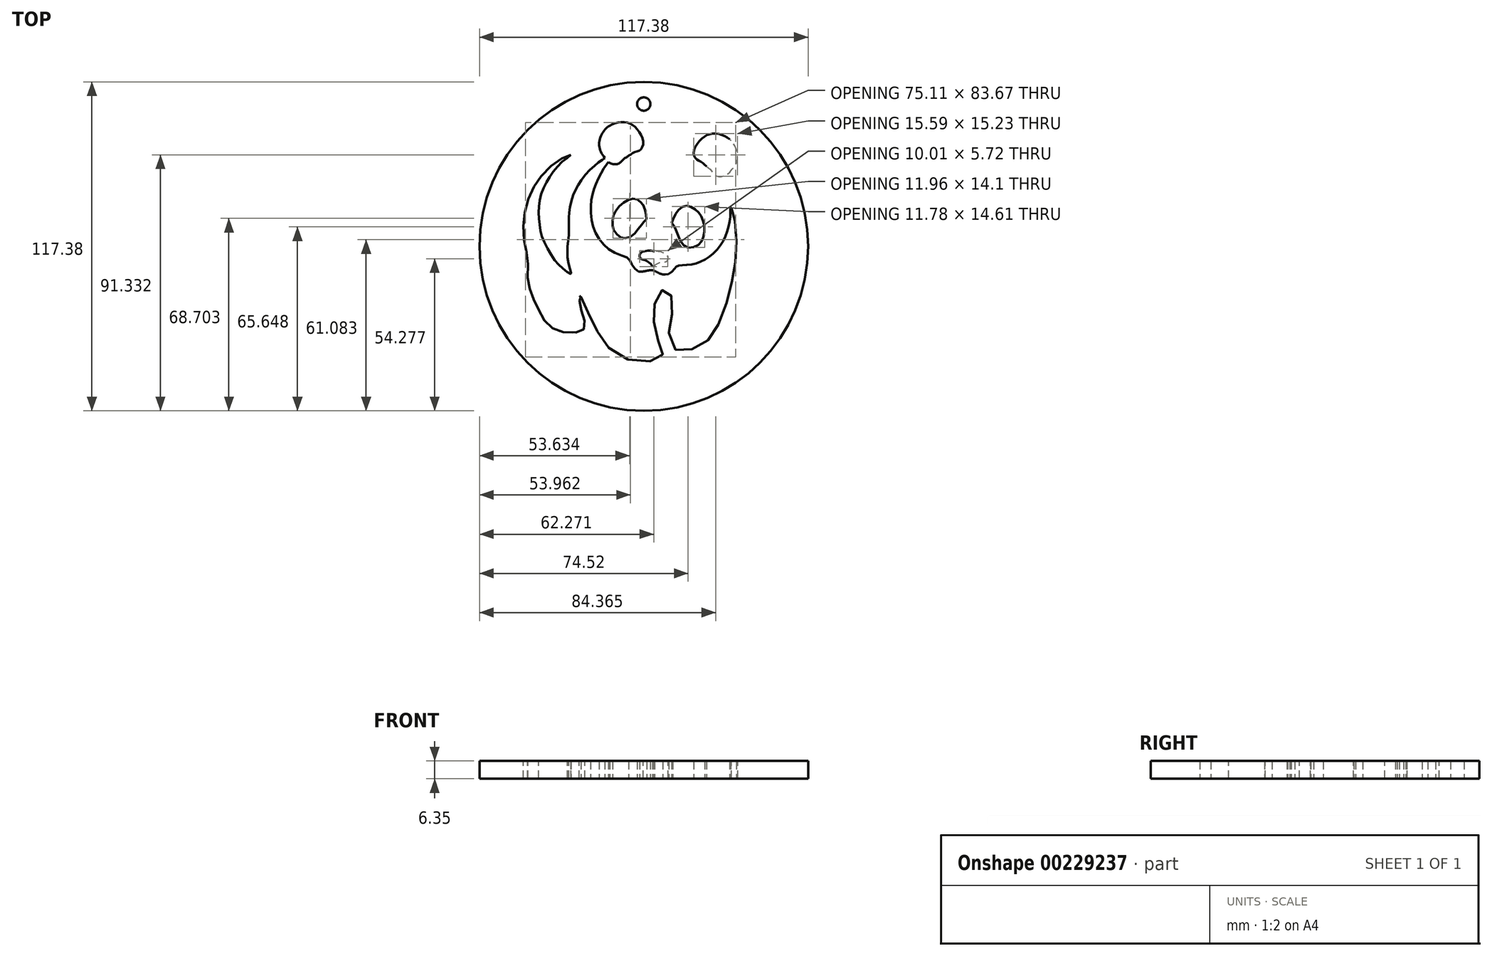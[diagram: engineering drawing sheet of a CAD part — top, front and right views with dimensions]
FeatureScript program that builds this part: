
annotation { "Feature Type Name" : "Feature", "Feature Type Description" : "" }
export const myFeature = defineFeature(function(context is Context, id is Id, definition is map)
    precondition{}
    {
        {
            var Q0;
            Q0=qCreatedBy(makeId("Top.planeOp"),FACE);
            var sketch = newSketch(context, id + "F0", { "sketchPlane" : qUnion([Q0])});
            skFitSpline(sketch, "E0", {"points": [v(-9.45, -0.21) * mm, v(-9.65, 1.94) * mm, v(-10.1, 4.07) * mm, v(-11.24, 5.8) * mm, v(-12.39, 6.69) * mm, v(-13.82, 7.25) * mm, v(-16.1, 6.73) * mm, v(-18.02, 5.5) * mm, v(-19.95, 3.49) * mm, v(-21.27, 0.9) * mm, v(-21.48, -1.33) * mm, v(-21.32, -3.3) * mm, v(-20.37, -5.07) * mm, v(-18.44, -6.7) * mm, v(-16.78, -6.87) * mm, v(-14.6, -6.12) * mm, v(-12.36, -3.6) * mm, v(-11.05, -1.96) * mm, v(-10.27, -0.98) * mm, v(-9.45, -0.21) * mm]});
            skLineSegment(sketch, "E1", {"start": v(-7.13, -17.08) * mm, "end": v(-6.54, -11.5) * mm, "construction": true});
            skFitSpline(sketch, "E2", {"points": [v(-7.13, -17.08) * mm, v(-6.61, -16.68) * mm, v(-6.27, -16.39) * mm, v(-5.51, -15.93) * mm, v(-4.62, -15.58) * mm, v(-3.6, -15.41) * mm, v(-2.85, -15.39) * mm, v(-2.06, -15) * mm, v(-1.7, -14.33) * mm, v(-1.68, -13.65) * mm, v(-2.14, -12.86) * mm, v(-3.15, -12.2) * mm, v(-4.37, -11.82) * mm, v(-5.34, -11.65) * mm, v(-6.54, -11.5) * mm], "startDerivative": vector(8.27, 4.27) * mm, "endDerivative": vector(-8.57, -0.03) * mm});
            skFitSpline(sketch, "E3.MirrorCS", {"points": [v(-7.13, -17.08) * mm, v(-7.55, -16.58) * mm, v(-7.82, -16.22) * mm, v(-8.47, -15.61) * mm, v(-9.27, -15.08) * mm, v(-10.24, -14.7) * mm, v(-10.96, -14.52) * mm, v(-11.65, -13.98) * mm, v(-11.87, -13.25) * mm, v(-11.74, -12.59) * mm, v(-11.12, -11.9) * mm, v(-10, -11.48) * mm, v(-8.73, -11.36) * mm, v(-7.74, -11.4) * mm, v(-6.54, -11.5) * mm], "startDerivative": vector(-7.19, 5.91) * mm, "endDerivative": vector(8.37, -1.83) * mm});
            skLineSegment(sketch, "E4", {"start": v(12, 18.82) * mm, "end": v(20.22, 28.44) * mm, "construction": true});
            skFitSpline(sketch, "E5", {"points": [v(12, 18.82) * mm, v(12.77, 18.12) * mm, v(13.56, 17.43) * mm, v(14.25, 16.5) * mm, v(14.91, 15.73) * mm, v(15.82, 15.22) * mm, v(17.04, 15.04) * mm, v(18.74, 15.54) * mm, v(20.57, 17) * mm, v(22.03, 18.82) * mm, v(22.87, 20.59) * mm, v(23.15, 22.16) * mm, v(22.91, 24.11) * mm, v(22.24, 25.86) * mm, v(21.34, 27.32) * mm, v(20.22, 28.44) * mm], "startDerivative": vector(13.61, -13.3) * mm, "endDerivative": vector(-19.87, 13.26) * mm});
            skFitSpline(sketch, "E6.MirrorCS", {"points": [v(12, 18.82) * mm, v(11.19, 19.46) * mm, v(10.39, 20.14) * mm, v(9.37, 20.68) * mm, v(8.5, 21.21) * mm, v(7.85, 22.02) * mm, v(7.49, 23.2) * mm, v(7.7, 24.96) * mm, v(8.87, 27) * mm, v(10.44, 28.72) * mm, v(12.05, 29.83) * mm, v(13.56, 30.35) * mm, v(15.53, 30.42) * mm, v(17.35, 30.04) * mm, v(18.93, 29.37) * mm, v(20.22, 28.44) * mm], "startDerivative": vector(-15.26, 11.37) * mm, "endDerivative": vector(16.2, -17.55) * mm});
            skFitSpline(sketch, "E7", {"points": [v(-15.77, 22.56) * mm, v(-14.87, 23.07) * mm, v(-13.98, 23.62) * mm, v(-12.9, 24) * mm, v(-11.96, 24.41) * mm, v(-11.2, 25.12) * mm, v(-10.67, 26.24) * mm, v(-10.63, 28) * mm, v(-11.48, 30.19) * mm, v(-12.79, 32.12) * mm, v(-14.22, 33.45) * mm, v(-15.64, 34.18) * mm, v(-17.57, 34.54) * mm, v(-19.43, 34.42) * mm, v(-21.1, 34) * mm, v(-22.5, 33.26) * mm], "startDerivative": vector(16.75, 9.03) * mm, "endDerivative": vector(-18.57, -15.02) * mm});
            skFitSpline(sketch, "E8.MirrorCS", {"points": [v(-15.77, 22.56) * mm, v(-16.63, 21.97) * mm, v(-17.51, 21.4) * mm, v(-18.33, 20.59) * mm, v(-19.1, 19.92) * mm, v(-20.07, 19.54) * mm, v(-21.3, 19.55) * mm, v(-22.91, 20.28) * mm, v(-24.5, 22) * mm, v(-25.7, 24.01) * mm, v(-26.26, 25.88) * mm, v(-26.31, 27.47) * mm, v(-25.8, 29.37) * mm, v(-24.88, 31) * mm, v(-23.78, 32.32) * mm, v(-22.5, 33.26) * mm], "startDerivative": vector(-15.4, -11.18) * mm, "endDerivative": vector(21.58, 10.23) * mm});
            skFitSpline(sketch, "E9", {"points": [v(-22.97, 20.33) * mm, v(-23.35, 19.77) * mm, v(-24.07, 18.85) * mm, v(-25.06, 17.32) * mm, v(-26.24, 15.22) * mm, v(-27.42, 12.67) * mm, v(-28.12, 10.8) * mm, v(-28.63, 9) * mm, v(-29.16, 5.98) * mm, v(-29.33, 3.24) * mm, v(-29, -0.56) * mm, v(-28.2, -3.56) * mm, v(-26.63, -6.7) * mm, v(-24.33, -9.54) * mm, v(-21.64, -11.65) * mm, v(-17.98, -13.23) * mm, v(-16.1, -13.91) * mm, v(-15.16, -15.07) * mm, v(-14.66, -16.27) * mm, v(-13.47, -17.96) * mm, v(-12.17, -18.8) * mm, v(-10.25, -18.71) * mm, v(-8.8, -18.43) * mm, v(-7.33, -18.35) * mm], "startDerivative": vector(-14.05, -22.2) * mm, "endDerivative": vector(35.9, -3.85) * mm});
            skFitSpline(sketch, "E10", {"points": [v(-7.33, -18.35) * mm, v(-6.65, -18.52) * mm, v(-5.91, -18.87) * mm, v(-5.28, -19.2) * mm, v(-4.42, -19.57) * mm, v(-3.54, -19.83) * mm, v(-2.7, -19.9) * mm, v(-1.5, -19.71) * mm, v(0.34, -18.14) * mm, v(0.9, -17.44) * mm, v(1.6, -16.87) * mm, v(2.49, -16.64) * mm, v(4.5, -16.48) * mm, v(7.18, -16.17) * mm, v(9.84, -15.3) * mm, v(12.44, -13.88) * mm, v(14.95, -11.87) * mm, v(17.14, -9.23) * mm, v(18.72, -6.45) * mm, v(19.8, -3.14) * mm, v(20.4, -0.4) * mm, v(20.5, 2.19) * mm, v(20.64, 4.02) * mm], "startDerivative": vector(22.76, -4.55) * mm, "endDerivative": vector(10, 38.6) * mm});
            skFitSpline(sketch, "E11", {"points": [v(20.64, 4.02) * mm, v(21.2, 3.69) * mm, v(21.77, 1.66) * mm, v(22.13, -0.21) * mm, v(22.44, -2.66) * mm, v(22.69, -7.22) * mm, v(22.62, -11.45) * mm, v(22.31, -15.8) * mm, v(21.5, -20.19) * mm, v(20.93, -23.17) * mm, v(20.14, -26.46) * mm, v(18.07, -33.4) * mm, v(16.45, -37.25) * mm, v(14.83, -40.35) * mm, v(12.93, -42.9) * mm, v(10.64, -44.82) * mm, v(7.36, -46.34) * mm, v(4.4, -46.96) * mm, v(1.93, -46.94) * mm, v(0, -46.07) * mm, v(-1.45, -42.28) * mm, v(-0.97, -38.56) * mm, v(-0.39, -35.07) * mm, v(-0.1, -32.63) * mm, v(-0.2, -28.84) * mm, v(-1.07, -26.34) * mm, v(-2.24, -25.37) * mm, v(-3.28, -25.17) * mm, v(-4.92, -26.4) * mm, v(-5.99, -28.5) * mm, v(-6.74, -31.2) * mm, v(-6.82, -34) * mm, v(-6.71, -37.34) * mm, v(-6.15, -40.5) * mm, v(-4.87, -44.43) * mm, v(-3.86, -46.44) * mm, v(-3.58, -47.98) * mm, v(-3.9, -49.07) * mm, v(-5.6, -50.27) * mm, v(-9, -50.97) * mm, v(-13.7, -50.8) * mm, v(-18.32, -49.26) * mm, v(-22.46, -46.36) * mm, v(-24.72, -43.76) * mm, v(-27.06, -40.02) * mm, v(-29.02, -36.25) * mm, v(-30.7, -32.5) * mm, v(-32.06, -29.5) * mm, v(-32.79, -27.9) * mm], "startDerivative": vector(61.87, -18.92) * mm, "endDerivative": vector(-42.49, 93.36) * mm});
            skFitSpline(sketch, "E12", {"points": [v(-24.32, 21.75) * mm, v(-25.03, 21.24) * mm, v(-26.64, 20.08) * mm, v(-29.05, 18.03) * mm, v(-32.02, 14.73) * mm, v(-34.02, 11.66) * mm, v(-35.32, 9.08) * mm, v(-36.47, 5.26) * mm, v(-36.97, 2.14) * mm, v(-37.1, -0.08) * mm, v(-37.1, -3.33) * mm, v(-37.25, -7.22) * mm, v(-37.62, -10.3) * mm, v(-37.62, -13.25) * mm, v(-37.09, -16.68) * mm, v(-36.4, -19) * mm, v(-36.17, -19.66) * mm], "startDerivative": vector(-18.22, -13.24) * mm, "endDerivative": vector(6.63, -17.87) * mm});
            skFitSpline(sketch, "E13", {"points": [v(-36.17, -19.66) * mm, v(-37.17, -19.34) * mm, v(-39.33, -17.57) * mm, v(-41.91, -15.08) * mm, v(-44.63, -10.78) * mm, v(-46.65, -6.43) * mm, v(-47.47, -2.74) * mm, v(-47.9, 1.43) * mm, v(-47.7, 5.49) * mm, v(-46.7, 9.64) * mm, v(-44.78, 13.77) * mm, v(-42.2, 17.47) * mm, v(-38.94, 20.88) * mm, v(-36.43, 22.89) * mm], "startDerivative": vector(-23.37, 4.1) * mm, "endDerivative": vector(19.95, 27.92) * mm});
            skFitSpline(sketch, "E14", {"points": [v(-36.43, 22.89) * mm, v(-37.28, 22.89) * mm, v(-40.48, 21) * mm, v(-43.59, 18.82) * mm, v(-46.85, 15.48) * mm, v(-49.03, 12.5) * mm, v(-50.79, 9.03) * mm, v(-52.27, 4.97) * mm, v(-53.11, 0.7) * mm, v(-53.37, -3.4) * mm, v(-53.04, -7.85) * mm, v(-52.4, -11.56) * mm, v(-51.8, -13.98) * mm, v(-51.87, -18.35) * mm, v(-51.73, -22) * mm, v(-51.13, -24.57) * mm, v(-50.23, -27.29) * mm, v(-49.03, -30.1) * mm, v(-48.1, -32.08) * mm, v(-46.42, -35.44) * mm, v(-44.08, -38.16) * mm, v(-42.24, -39.43) * mm, v(-39.15, -40.44) * mm, v(-35.3, -40.64) * mm, v(-32.77, -40.1) * mm, v(-31.9, -39.48) * mm, v(-31.4, -38.25) * mm, v(-31.54, -36.28) * mm, v(-32.36, -33.6) * mm, v(-32.98, -31.66) * mm, v(-33.32, -29.34) * mm, v(-33.34, -27.9) * mm, v(-33.11, -27.62) * mm, v(-32.79, -27.9) * mm], "startDerivative": vector(33.36, 55.45) * mm, "endDerivative": vector(28.2, -34.87) * mm});
            skFitSpline(sketch, "E15", {"points": [v(-12.17, -18.8) * mm, v(-12.17, -19.91) * mm, v(-11.64, -21.1) * mm, v(-10.44, -22.27) * mm, v(-9.07, -22.97) * mm, v(-7.54, -23.2) * mm, v(-5.62, -23.06) * mm, v(-4.04, -22.29) * mm, v(-3.16, -21.11) * mm, v(-2.7, -19.9) * mm], "startDerivative": vector(-1, -11.74) * mm, "endDerivative": vector(4.08, 11.96) * mm});
            skFitSpline(sketch, "E16", {"points": [v(-11.77, -18.86) * mm, v(-11.55, -19.75) * mm, v(-9.53, -20.14) * mm, v(-7.44, -20.46) * mm, v(-5.68, -20.62) * mm, v(-4.42, -20.7) * mm, v(-3.54, -20.7) * mm, v(-3.08, -19.88) * mm], "startDerivative": vector(-0.78, -11.29) * mm, "endDerivative": vector(3.47, 9.57) * mm});
            skFitSpline(sketch, "E17", {"points": [v(-0.43, -1.48) * mm, v(0, -0.38) * mm, v(0.98, 1.71) * mm, v(2.13, 3.26) * mm, v(3.5, 4.34) * mm, v(5.04, 4.62) * mm, v(6.36, 4.34) * mm, v(8, 3.4) * mm, v(9.25, 2.27) * mm, v(10.13, 0.98) * mm, v(10.82, -0.64) * mm, v(11.3, -2.77) * mm, v(11.2, -5.43) * mm, v(10.62, -7.27) * mm, v(9.68, -8.77) * mm, v(8.37, -9.66) * mm, v(6.37, -10.3) * mm, v(4.35, -9.77) * mm, v(2.75, -7.91) * mm, v(1.76, -5.56) * mm, v(0.87, -3.5) * mm, v(0.3, -2.37) * mm, v(-0.43, -1.48) * mm]});
            skArc(sketch, "E18.filletArc", {"start": v(-36.63, -19.56) * mm, "mid": v(-36.38, -19.49) * mm, "end": v(-36.32, -19.23) * mm});
            skArc(sketch, "E19.filletArc", {"start": v(20.95, 3.9) * mm, "mid": v(20.72, 3.91) * mm, "end": v(20.58, 3.73) * mm});
            skSolve(sketch);
        }
        {
            var Q0;
            Q0=qCreatedBy(makeId("Top.planeOp"),FACE);
            var sketch = newSketch(context, id + "F1", { "sketchPlane" : qUnion([Q0])});
            skCircle(sketch, "E20", {"center": v(-10.37, -9.81) * mm, "radius": 58.69 * mm});
            skCircle(sketch, "E21", {"center": v(-10.37, 40.99) * mm, "radius": 2.38 * mm});
            skSolve(sketch);
        }
        {
            var Q0;
            Q0 = qSketchRegion(id + "F1", true);
            extrude(context, id + "F2", {"entities" : qUnion([Q0]), "depth" : 6.35 * mm});
        }
        {
            var Q0;
            Q0 = qSketchRegion(id + "F0", true);
            extrude(context, id + "F3", {"entities" : qUnion([Q0]), "operationType" : NewBodyOperationType.REMOVE, "depth" : 6.35 * mm});
        }
    });
